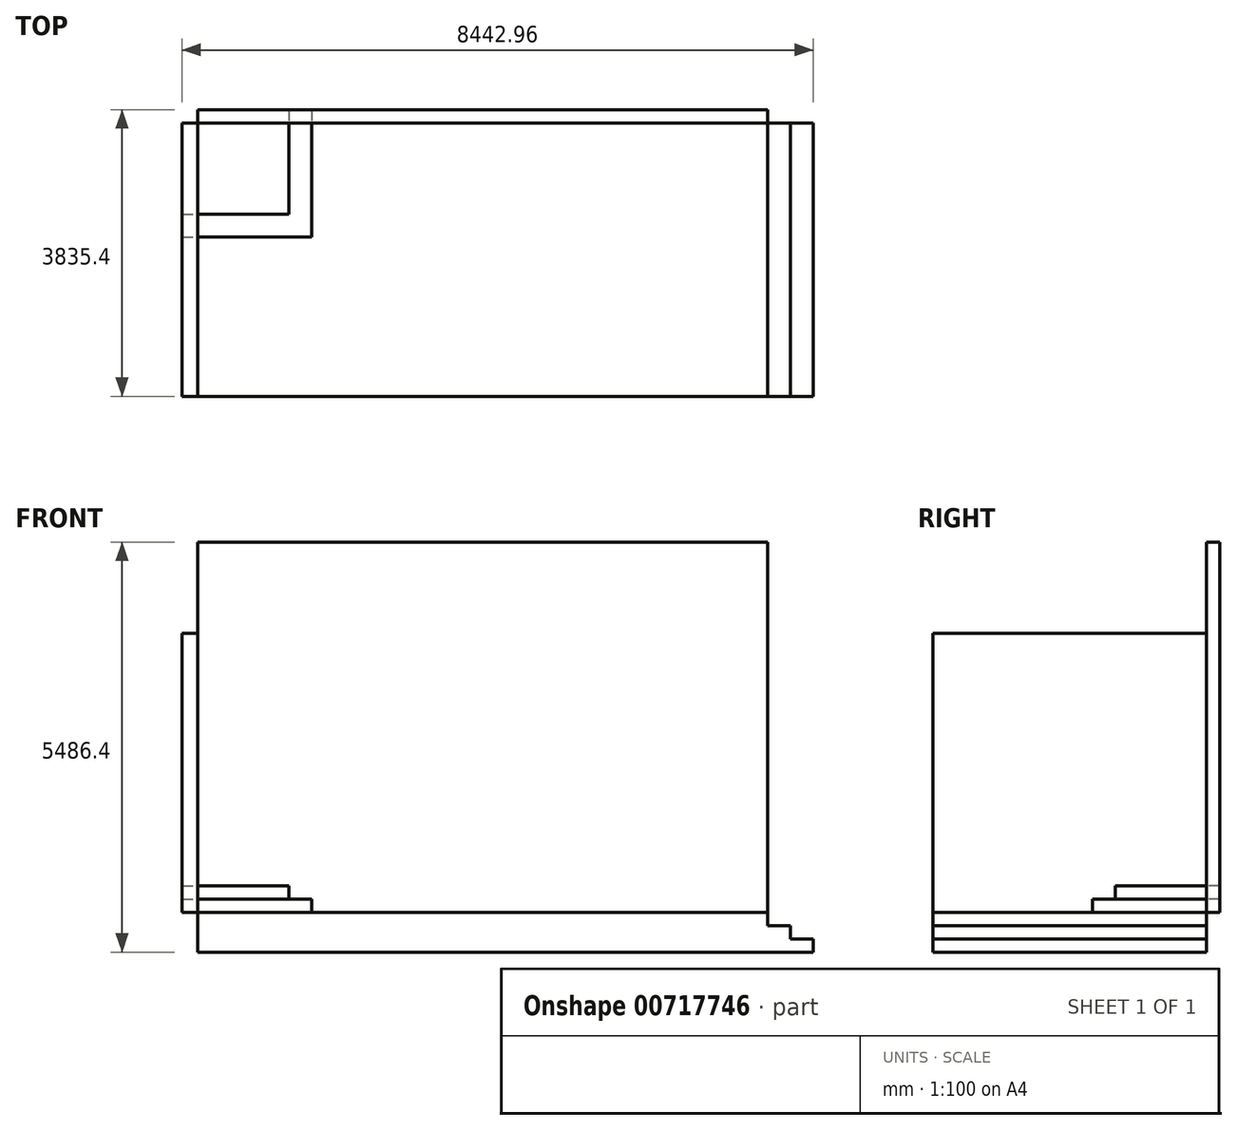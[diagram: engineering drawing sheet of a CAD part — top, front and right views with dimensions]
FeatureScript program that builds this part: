
annotation { "Feature Type Name" : "Feature", "Feature Type Description" : "" }
export const myFeature = defineFeature(function(context is Context, id is Id, definition is map)
    precondition{}
    {
        {
            var Q0;
            Q0=qCreatedBy(makeId("Top.planeOp"),FACE);
            var sketch = newSketch(context, id + "F0", { "sketchPlane" : qUnion([Q0])});
            skLineSegment(sketch, "E0.bottom", {"start": v(3810, -1828.8) * mm, "end": v(-3810, -1828.8) * mm});
            skLineSegment(sketch, "E0.top", {"start": v(3810, 1828.8) * mm, "end": v(-3810, 1828.8) * mm});
            skLineSegment(sketch, "E0.left", {"start": v(3810, -1828.8) * mm, "end": v(3810, 1828.8) * mm});
            skLineSegment(sketch, "E0.right", {"start": v(-3810, -1828.8) * mm, "end": v(-3810, 1828.8) * mm});
            skPoint(sketch, "E0.middle", {"position": v(0, 0) * mm});
            skSolve(sketch);
        }
        {
            var Q0;
            Q0=makeQuery(id+"F0.imprint","IMPRINT",FACE,{"disambiguationData":[TD([[makeQuery(id+"F0.imprint","IMPRINT",EDGE,{"derivedFrom":sQuery(id+"F0.wireOp",EDGE,"E0.bottom")}),-1.0]])]});
            extrude(context, id + "F1", {"entities" : qUnion([Q0]), "depth" : 533.4 * mm, "offsetDistance" : 30.48 * mm});
        }
        {
            var Q0;
            Q0=makeQuery(id+"F1.opExtrude","CAP_FACE",FACE,{"disambiguationData":[OSD([sQuery(id+"F0.wireOp",EDGE,"E0.bottom"),sQuery(id+"F0.wireOp",EDGE,"E0.top"),sQuery(id+"F0.wireOp",EDGE,"E0.left"),sQuery(id+"F0.wireOp",EDGE,"E0.right")])],"isStart":true});
            var sketch = newSketch(context, id + "F2", { "sketchPlane" : qUnion([Q0])});
            skLineSegment(sketch, "E1.bottom", {"start": v(-3810, -1828.8) * mm, "end": v(4419.6, -1828.8) * mm});
            skLineSegment(sketch, "E1.top", {"start": v(-3810, 1828.8) * mm, "end": v(4419.6, 1828.8) * mm});
            skLineSegment(sketch, "E1.left", {"start": v(-3810, -1828.8) * mm, "end": v(-3810, 1828.8) * mm});
            skLineSegment(sketch, "E1.right", {"start": v(4419.6, -1828.8) * mm, "end": v(4419.6, 1828.8) * mm});
            skSolve(sketch);
        }
        {
            var Q0;
            {var subQ4=sQuery(id+"F2.wireOp",EDGE,"E1.top");Q0=makeQuery(id+"F2.imprint","IMPRINT",FACE,{"disambiguationData":[TD([[makeQuery(id+"F2.imprint","IMPRINT",EDGE,{"derivedFrom":subQ4}),-1.0]])]});}
            extrude(context, id + "F3", {"entities" : qUnion([Q0]), "operationType" : NewBodyOperationType.ADD, "oppositeDirection" : true, "depth" : 177.8 * mm, "offsetDistance" : 30.48 * mm});
        }
        {
            var Q0;
            Q0=makeQuery(id+"F1.opExtrude","CAP_FACE",FACE,{"disambiguationData":[OSD([sQuery(id+"F0.wireOp",EDGE,"E0.bottom"),sQuery(id+"F0.wireOp",EDGE,"E0.top"),sQuery(id+"F0.wireOp",EDGE,"E0.left"),sQuery(id+"F0.wireOp",EDGE,"E0.right")])],"isStart":false});
            var sketch = newSketch(context, id + "F4", { "sketchPlane" : qUnion([Q0])});
            skLineSegment(sketch, "E2.bottom", {"start": v(-3810, 1828.8) * mm, "end": v(-2590.8, 1828.8) * mm});
            skLineSegment(sketch, "E2.top", {"start": v(-3810, 609.6) * mm, "end": v(-2590.8, 609.6) * mm});
            skLineSegment(sketch, "E2.left", {"start": v(-3810, 1828.8) * mm, "end": v(-3810, 609.6) * mm});
            skLineSegment(sketch, "E2.right", {"start": v(-2590.8, 1828.8) * mm, "end": v(-2590.8, 609.6) * mm});
            skSolve(sketch);
        }
        {
            var Q0;
            Q0=makeQuery(id+"F4.imprint","IMPRINT",FACE,{"disambiguationData":[TD([[makeQuery(id+"F4.imprint","IMPRINT",EDGE,{"derivedFrom":sQuery(id+"F4.wireOp",EDGE,"E2.bottom")}),1.0]])]});
            extrude(context, id + "F5", {"entities" : qUnion([Q0]), "operationType" : NewBodyOperationType.ADD, "depth" : 355.6 * mm, "offsetDistance" : 30.48 * mm});
        }
        {
            var Q0;
            {var subQ0=sQuery(id+"F0.wireOp",EDGE,"E0.right");var subQ1=sQuery(id+"F0.wireOp",EDGE,"E0.left");var subQ2=sQuery(id+"F0.wireOp",EDGE,"E0.top");var subQ3=sQuery(id+"F0.wireOp",EDGE,"E0.bottom");Q0=makeQuery(id+"F3.boolean.opBoolean","MERGE",FACE,{"derivedFrom":[makeQuery(id+"F1.opExtrude","CAP_FACE",FACE,{"disambiguationData":[OSD([subQ3,subQ2,subQ1,subQ0])],"isStart":true}),makeQuery(id+"F3.opExtrude","CAP_FACE",FACE,{"disambiguationData":[OSD([subQ3,subQ2,subQ1,subQ0,sQuery(id+"F2.wireOp",EDGE,"E1.bottom"),sQuery(id+"F2.wireOp",EDGE,"E1.top"),sQuery(id+"F2.wireOp",EDGE,"E1.left"),sQuery(id+"F2.wireOp",EDGE,"E1.right")])],"isStart":true})]});}
            var sketch = newSketch(context, id + "F6", { "sketchPlane" : qUnion([Q0])});
            skLineSegment(sketch, "E3.bottom", {"start": v(-3810, -1828.8) * mm, "end": v(-2286, -1828.8) * mm});
            skLineSegment(sketch, "E3.top", {"start": v(-3810, -304.8) * mm, "end": v(-2286, -304.8) * mm});
            skLineSegment(sketch, "E3.left", {"start": v(-3810, -1828.8) * mm, "end": v(-3810, -304.8) * mm});
            skLineSegment(sketch, "E3.right", {"start": v(-2286, -1828.8) * mm, "end": v(-2286, -304.8) * mm});
            skSolve(sketch);
        }
        {
            var Q0;
            Q0=makeQuery(id+"F6.imprint","IMPRINT",FACE,{"disambiguationData":[TD([[makeQuery(id+"F6.imprint","IMPRINT",EDGE,{"derivedFrom":sQuery(id+"F6.wireOp",EDGE,"E3.bottom")}),-1.0]])]});
            extrude(context, id + "F7", {"entities" : qUnion([Q0]), "operationType" : NewBodyOperationType.ADD, "oppositeDirection" : true, "depth" : 711.2 * mm, "offsetDistance" : 30.48 * mm});
        }
        {
            var Q0;
            Q0=makeQuery(id+"F7.boolean.opBoolean","MERGE",FACE,{"derivedFrom":[makeQuery(id+"F5.boolean.opBoolean","MERGE",FACE,{"derivedFrom":[makeQuery(id+"F3.boolean.opBoolean","MERGE",FACE,{"derivedFrom":[makeQuery(id+"F1.opExtrude","SWEPT_FACE",FACE,{"disambiguationData":[OSD([sQuery(id+"F0.wireOp",EDGE,"E0.top")])]}),makeQuery(id+"F3.opExtrude","SWEPT_FACE",FACE,{"disambiguationData":[OSD([sQuery(id+"F2.wireOp",EDGE,"E1.bottom")])]})]}),makeQuery(id+"F5.opExtrude","SWEPT_FACE",FACE,{"disambiguationData":[OSD([sQuery(id+"F4.wireOp",EDGE,"E2.bottom")])]})]}),makeQuery(id+"F7.opExtrude","SWEPT_FACE",FACE,{"disambiguationData":[OSD([sQuery(id+"F6.wireOp",EDGE,"E3.bottom")])]})]});
            var sketch = newSketch(context, id + "F8", { "sketchPlane" : qUnion([Q0])});
            skLineSegment(sketch, "E4.bottom", {"start": v(3810, 0) * mm, "end": v(-3810, 0) * mm});
            skLineSegment(sketch, "E4.top", {"start": v(3810, 5486.4) * mm, "end": v(-3810, 5486.4) * mm});
            skLineSegment(sketch, "E4.left", {"start": v(3810, 0) * mm, "end": v(3810, 5486.4) * mm});
            skLineSegment(sketch, "E4.right", {"start": v(-3810, 0) * mm, "end": v(-3810, 5486.4) * mm});
            skSolve(sketch);
        }
        {
            var Q0;
            {var subQ5=sQuery(id+"F8.wireOp",EDGE,"E4.top");Q0=makeQuery(id+"F8.imprint","IMPRINT",FACE,{"disambiguationData":[TD([[makeQuery(id+"F8.imprint","IMPRINT",EDGE,{"derivedFrom":subQ5}),1.0]])]});}
            extrude(context, id + "F9", {"entities" : qUnion([Q0]), "depth" : 177.8 * mm, "offsetDistance" : 30.48 * mm});
        }
        {
            var Q0;
            Q0=makeQuery(id+"F7.boolean.opBoolean","MERGE",FACE,{"derivedFrom":[makeQuery(id+"F5.boolean.opBoolean","MERGE",FACE,{"derivedFrom":[makeQuery(id+"F3.boolean.opBoolean","MERGE",FACE,{"derivedFrom":[makeQuery(id+"F1.opExtrude","SWEPT_FACE",FACE,{"disambiguationData":[OSD([sQuery(id+"F0.wireOp",EDGE,"E0.right")])]}),makeQuery(id+"F3.opExtrude","SWEPT_FACE",FACE,{"disambiguationData":[OSD([sQuery(id+"F2.wireOp",EDGE,"E1.left")])]})]}),makeQuery(id+"F5.opExtrude","SWEPT_FACE",FACE,{"disambiguationData":[OSD([sQuery(id+"F4.wireOp",EDGE,"E2.left")])]})]}),makeQuery(id+"F7.opExtrude","SWEPT_FACE",FACE,{"disambiguationData":[OSD([sQuery(id+"F6.wireOp",EDGE,"E3.left")])]})]});
            var sketch = newSketch(context, id + "F10", { "sketchPlane" : qUnion([Q0])});
            skLineSegment(sketch, "E5.bottom", {"start": v(-1828.8, 0) * mm, "end": v(1828.8, 0) * mm});
            skLineSegment(sketch, "E5.top", {"start": v(-1828.8, 4267.2) * mm, "end": v(1828.8, 4267.2) * mm});
            skLineSegment(sketch, "E5.left", {"start": v(-1828.8, 0) * mm, "end": v(-1828.8, 4267.2) * mm});
            skLineSegment(sketch, "E5.right", {"start": v(1828.8, 0) * mm, "end": v(1828.8, 4267.2) * mm});
            skSolve(sketch);
        }
        {
            var Q0;
            {var subQ5=sQuery(id+"F10.wireOp",EDGE,"E5.top");Q0=makeQuery(id+"F10.imprint","IMPRINT",FACE,{"disambiguationData":[TD([[makeQuery(id+"F10.imprint","IMPRINT",EDGE,{"derivedFrom":subQ5}),-1.0]])]});}
            extrude(context, id + "F11", {"entities" : qUnion([Q0]), "depth" : 213.36 * mm, "offsetDistance" : 30.48 * mm});
        }
        {
            var Q0;
            Q0=makeQuery(id+"F3.opExtrude","CAP_FACE",FACE,{"disambiguationData":[OSD([sQuery(id+"F0.wireOp",EDGE,"E0.left"),sQuery(id+"F2.wireOp",EDGE,"E1.bottom"),sQuery(id+"F2.wireOp",EDGE,"E1.top"),sQuery(id+"F2.wireOp",EDGE,"E1.right")])],"isStart":false});
            var sketch = newSketch(context, id + "F12", { "sketchPlane" : qUnion([Q0])});
            skLineSegment(sketch, "E6.bottom", {"start": v(3810, -1828.8) * mm, "end": v(4114.8, -1828.8) * mm});
            skLineSegment(sketch, "E6.top", {"start": v(3810, 1828.8) * mm, "end": v(4114.8, 1828.8) * mm});
            skLineSegment(sketch, "E6.left", {"start": v(3810, -1828.8) * mm, "end": v(3810, 1828.8) * mm});
            skLineSegment(sketch, "E6.right", {"start": v(4114.8, -1828.8) * mm, "end": v(4114.8, 1828.8) * mm});
            skSolve(sketch);
        }
        {
            var Q0;
            Q0=makeQuery(id+"F12.imprint","IMPRINT",FACE,{"disambiguationData":[TD([[makeQuery(id+"F12.imprint","IMPRINT",EDGE,{"derivedFrom":sQuery(id+"F12.wireOp",EDGE,"E6.bottom")}),1.0]])]});
            extrude(context, id + "F13", {"entities" : qUnion([Q0]), "operationType" : NewBodyOperationType.ADD, "depth" : 177.8 * mm, "offsetDistance" : 30.48 * mm});
        }
    });
